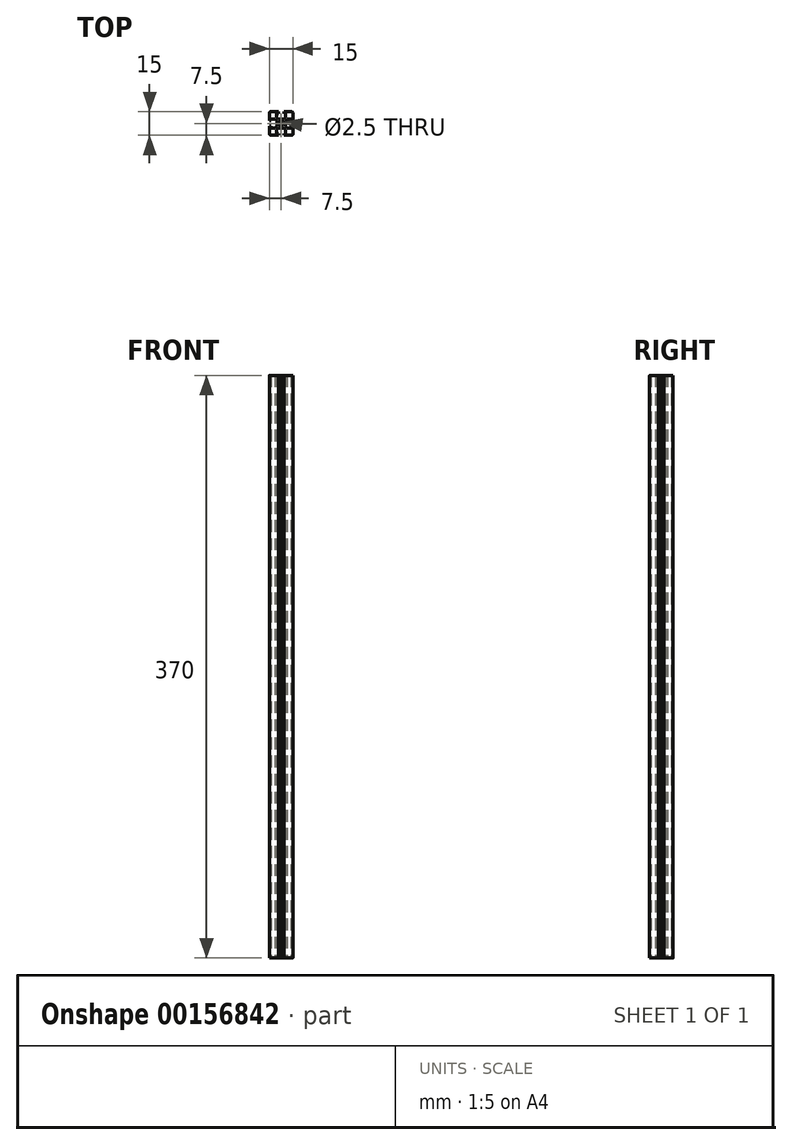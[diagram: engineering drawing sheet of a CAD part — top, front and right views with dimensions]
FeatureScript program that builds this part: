
annotation { "Feature Type Name" : "Feature", "Feature Type Description" : "" }
export const myFeature = defineFeature(function(context is Context, id is Id, definition is map)
    precondition{}
    {
        {
            var Q0;
            Q0=qCreatedBy(makeId("Top.planeOp"),FACE);
            var sketch = newSketch(context, id + "F0", { "sketchPlane" : qUnion([Q0])});
            skLineSegment(sketch, "E0.bottom", {"start": v(6.5, -7.5) * mm, "end": v(1.7, -7.5) * mm});
            skLineSegment(sketch, "E0.top", {"start": v(6.5, 7.5) * mm, "end": v(1.7, 7.5) * mm});
            skLineSegment(sketch, "E0.left", {"start": v(7.5, -6.5) * mm, "end": v(7.5, -1.7) * mm});
            skLineSegment(sketch, "E0.right", {"start": v(-7.5, -6.5) * mm, "end": v(-7.5, -1.7) * mm});
            skPoint(sketch, "E0.middle", {"position": v(0, 0) * mm});
            skPoint(sketch, "E1.visualSharp", {"position": v(7.5, 7.5) * mm});
            skArc(sketch, "E1.filletArc", {"start": v(7.5, 6.5) * mm, "mid": v(7.2, 7.2) * mm, "end": v(6.5, 7.5) * mm});
            skPoint(sketch, "E2.visualSharp", {"position": v(-7.5, 7.5) * mm});
            skArc(sketch, "E2.filletArc", {"start": v(-6.5, 7.5) * mm, "mid": v(-7.2, 7.2) * mm, "end": v(-7.5, 6.5) * mm});
            skPoint(sketch, "E3.visualSharp", {"position": v(-7.5, -7.5) * mm});
            skArc(sketch, "E3.filletArc", {"start": v(-7.5, -6.5) * mm, "mid": v(-7.2, -7.2) * mm, "end": v(-6.5, -7.5) * mm});
            skPoint(sketch, "E4.visualSharp", {"position": v(7.5, -7.5) * mm});
            skArc(sketch, "E4.filletArc", {"start": v(6.5, -7.5) * mm, "mid": v(7.2, -7.2) * mm, "end": v(7.5, -6.5) * mm});
            skCircle(sketch, "E5", {"center": v(0, 0) * mm, "radius": 1.25 * mm});
            skLineSegment(sketch, "E6", {"start": v(-1.7, 7.5) * mm, "end": v(-1.7, 6.4) * mm});
            skLineSegment(sketch, "E7", {"start": v(-1.7, 6.4) * mm, "end": v(-2.85, 6.4) * mm});
            skLineSegment(sketch, "E8", {"start": v(-2.85, 6.4) * mm, "end": v(-2.85, 3.8) * mm});
            skLineSegment(sketch, "E9", {"start": v(-2.85, 3.8) * mm, "end": v(-1.7, 2.8) * mm});
            skLineSegment(sketch, "E10", {"start": v(-1.7, 2.8) * mm, "end": v(-0.52, 2.8) * mm});
            skLineSegment(sketch, "E11", {"start": v(-0.52, 2.8) * mm, "end": v(0, 2.5) * mm});
            skLineSegment(sketch, "E12", {"start": v(0, 7.5) * mm, "end": v(0, 1.25) * mm, "construction": true});
            skLineSegment(sketch, "E13.MirrorCS", {"start": v(1.7, 7.5) * mm, "end": v(1.7, 6.4) * mm});
            skLineSegment(sketch, "E14.MirrorCS", {"start": v(1.7, 6.4) * mm, "end": v(2.85, 6.4) * mm});
            skLineSegment(sketch, "E15.MirrorCS", {"start": v(2.85, 6.4) * mm, "end": v(2.85, 3.8) * mm});
            skLineSegment(sketch, "E16.MirrorCS", {"start": v(2.85, 3.8) * mm, "end": v(1.7, 2.8) * mm});
            skLineSegment(sketch, "E17.MirrorCS", {"start": v(1.7, 2.8) * mm, "end": v(0.52, 2.8) * mm});
            skLineSegment(sketch, "E18.MirrorCS", {"start": v(0.52, 2.8) * mm, "end": v(0, 2.5) * mm});
            skLineSegment(sketch, "E19.1.0", {"start": v(-7.5, -1.7) * mm, "end": v(-6.4, -1.7) * mm});
            skLineSegment(sketch, "E19.1.1", {"start": v(-6.4, -1.7) * mm, "end": v(-6.4, -2.85) * mm});
            skLineSegment(sketch, "E19.1.2", {"start": v(-6.4, -2.85) * mm, "end": v(-3.8, -2.85) * mm});
            skLineSegment(sketch, "E19.1.3", {"start": v(-3.8, -2.85) * mm, "end": v(-2.8, -1.7) * mm});
            skLineSegment(sketch, "E19.1.4", {"start": v(-2.8, -1.7) * mm, "end": v(-2.8, -0.52) * mm});
            skLineSegment(sketch, "E19.1.5", {"start": v(-7.5, 1.7) * mm, "end": v(-6.4, 1.7) * mm});
            skLineSegment(sketch, "E19.1.6", {"start": v(-6.4, 1.7) * mm, "end": v(-6.4, 2.85) * mm});
            skLineSegment(sketch, "E19.1.7", {"start": v(-6.4, 2.85) * mm, "end": v(-3.8, 2.85) * mm});
            skLineSegment(sketch, "E19.1.8", {"start": v(-3.8, 2.85) * mm, "end": v(-2.8, 1.7) * mm});
            skLineSegment(sketch, "E19.1.9", {"start": v(-2.8, 1.7) * mm, "end": v(-2.8, 0.52) * mm});
            skLineSegment(sketch, "E19.1.10", {"start": v(-2.8, 0.52) * mm, "end": v(-2.5, 0) * mm});
            skLineSegment(sketch, "E19.1.11", {"start": v(-2.8, -0.52) * mm, "end": v(-2.5, 0) * mm});
            skLineSegment(sketch, "E19.2.0", {"start": v(1.7, -7.5) * mm, "end": v(1.7, -6.4) * mm});
            skLineSegment(sketch, "E19.2.1", {"start": v(1.7, -6.4) * mm, "end": v(2.85, -6.4) * mm});
            skLineSegment(sketch, "E19.2.2", {"start": v(2.85, -6.4) * mm, "end": v(2.85, -3.8) * mm});
            skLineSegment(sketch, "E19.2.3", {"start": v(2.85, -3.8) * mm, "end": v(1.7, -2.8) * mm});
            skLineSegment(sketch, "E19.2.4", {"start": v(1.7, -2.8) * mm, "end": v(0.52, -2.8) * mm});
            skLineSegment(sketch, "E19.2.5", {"start": v(-1.7, -7.5) * mm, "end": v(-1.7, -6.4) * mm});
            skLineSegment(sketch, "E19.2.6", {"start": v(-1.7, -6.4) * mm, "end": v(-2.85, -6.4) * mm});
            skLineSegment(sketch, "E19.2.7", {"start": v(-2.85, -6.4) * mm, "end": v(-2.85, -3.8) * mm});
            skLineSegment(sketch, "E19.2.8", {"start": v(-2.85, -3.8) * mm, "end": v(-1.7, -2.8) * mm});
            skLineSegment(sketch, "E19.2.9", {"start": v(-1.7, -2.8) * mm, "end": v(-0.52, -2.8) * mm});
            skLineSegment(sketch, "E19.2.10", {"start": v(-0.52, -2.8) * mm, "end": v(0, -2.5) * mm});
            skLineSegment(sketch, "E19.2.11", {"start": v(0.52, -2.8) * mm, "end": v(0, -2.5) * mm});
            skLineSegment(sketch, "E19.3.0", {"start": v(7.5, 1.7) * mm, "end": v(6.4, 1.7) * mm});
            skLineSegment(sketch, "E19.3.1", {"start": v(6.4, 1.7) * mm, "end": v(6.4, 2.85) * mm});
            skLineSegment(sketch, "E19.3.2", {"start": v(6.4, 2.85) * mm, "end": v(3.8, 2.85) * mm});
            skLineSegment(sketch, "E19.3.3", {"start": v(3.8, 2.85) * mm, "end": v(2.8, 1.7) * mm});
            skLineSegment(sketch, "E19.3.4", {"start": v(2.8, 1.7) * mm, "end": v(2.8, 0.52) * mm});
            skLineSegment(sketch, "E19.3.5", {"start": v(7.5, -1.7) * mm, "end": v(6.4, -1.7) * mm});
            skLineSegment(sketch, "E19.3.6", {"start": v(6.4, -1.7) * mm, "end": v(6.4, -2.85) * mm});
            skLineSegment(sketch, "E19.3.7", {"start": v(6.4, -2.85) * mm, "end": v(3.8, -2.85) * mm});
            skLineSegment(sketch, "E19.3.8", {"start": v(3.8, -2.85) * mm, "end": v(2.8, -1.7) * mm});
            skLineSegment(sketch, "E19.3.9", {"start": v(2.8, -1.7) * mm, "end": v(2.8, -0.52) * mm});
            skLineSegment(sketch, "E19.3.10", {"start": v(2.8, -0.52) * mm, "end": v(2.5, 0) * mm});
            skLineSegment(sketch, "E19.3.11", {"start": v(2.8, 0.52) * mm, "end": v(2.5, 0) * mm});
            skLineSegment(sketch, "E20.trimOffspring", {"start": v(-7.5, 1.7) * mm, "end": v(-7.5, 6.5) * mm});
            skLineSegment(sketch, "E21.trimOffspring", {"start": v(-1.7, -7.5) * mm, "end": v(-6.5, -7.5) * mm});
            skLineSegment(sketch, "E22.trimOffspring", {"start": v(7.5, 1.7) * mm, "end": v(7.5, 6.5) * mm});
            skLineSegment(sketch, "E23.trimOffspring", {"start": v(-1.7, 7.5) * mm, "end": v(-6.5, 7.5) * mm});
            skSolve(sketch);
        }
        {
            var Q0;
            Q0=qSketchRegion(id+"F0",true);
            extrude(context, id + "F1", {"entities" : qUnion([Q0]), "endBound" : BoundingType.SYMMETRIC, "depth" : 370 * mm});
        }
    });
